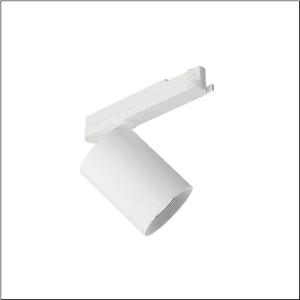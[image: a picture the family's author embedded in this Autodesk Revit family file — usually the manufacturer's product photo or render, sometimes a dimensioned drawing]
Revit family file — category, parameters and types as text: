
# Revit family: spot_21_51se13mbb5b
name_source: partatom
category: Lighting Fixtures
units: mm (PartAtom-declared; Revit-internal decimal feet)

## family parameters
Cut with Voids When Loaded = No
Host = Face
Light Source = No
Part Type = Normal
Room Calculation Point = No
Round Connector Dimension = Use Diameter
Shared = No

## types (1)
- --- (1 x LED, 5350 lm, 41.8 W, 3000K)
    Apparent Load = 42 VA
    CIE Flux Codes = 95 98 99 100 100
    Color Rendering = 90
    Color Temperature = 3000K
    Default Elevation = 1800 mm
    Description = Spot 21, directional spotlight, light control with lens, of PMMA, LED rated luminous flux: 5.140lm, light colour: 930, control gear: ECG Multilumen, with 3-phase adapter, mains connection: 220..240V, AC, 50/60Hz, of aluminium, traffic white (RAL 9016), length: 213mm, diameter: 105mm, protection rating (complete): IP20, insulation class (complete): insulation class I (protective earthing), certification: CE, impact resistance: IK02, permissible ambient temperature for indoor applications: -20..+40°C, packaging unit: 1 piece
    Height = 175 mm
    Lamp = 1 x LED
    Lamp Light Flux = 5350 lm
    Lamp Power = 41.8 W
    Lamp count = 1
    Length = 105 mm
    Luminous efficacy = 128 lm/W
    Manufacturer = Siteco
    ModVariant = No
    Model = 51SE13MBB5B
    Mounting Place = Ceiling
    Mounting Type = Pendant
    Number of Poles = 1
    OnlyDefault = Yes
    Power Factor = 1
    Product Name = Spot 21
    Product group = directional spotlight
    ProductGroupID = 905
    Protection Class = Protection class I
    Protection Degree = IP 20
    RLX_Detail_Level = 1
    RLX_Emergency_Light_Flux = 0 lm
    RLX_Emergency_Type = 0
    RLX_Emergency_Type_DB = No
    RlxData = <blob elided: 17665 chars, md5=a465b366>
    Socket = socket
    Standby Power = 0 W
    System Light Flux = 5350 lm
    System Power = 42 W
    Type Comments = factory setting: luminous flux: 100 % | (ON | ON | ON | ON) | 1050 mA
    Type Image = l_1003976.jpg
    URL = http://relux.com
    VarID = @adj_093681
    Voltage = 0 V
    Weight = 0.00 kg
    Width = 0 mm  [stored 0 ft]

note: [stored X ft] marks values corroborated as IEEE doubles in the binary element streams (Revit-internal decimal feet)

## geometry (parser evidence)
native form markers: Blend x4, Sweep x10
no freeform markers — native parametric forms only
